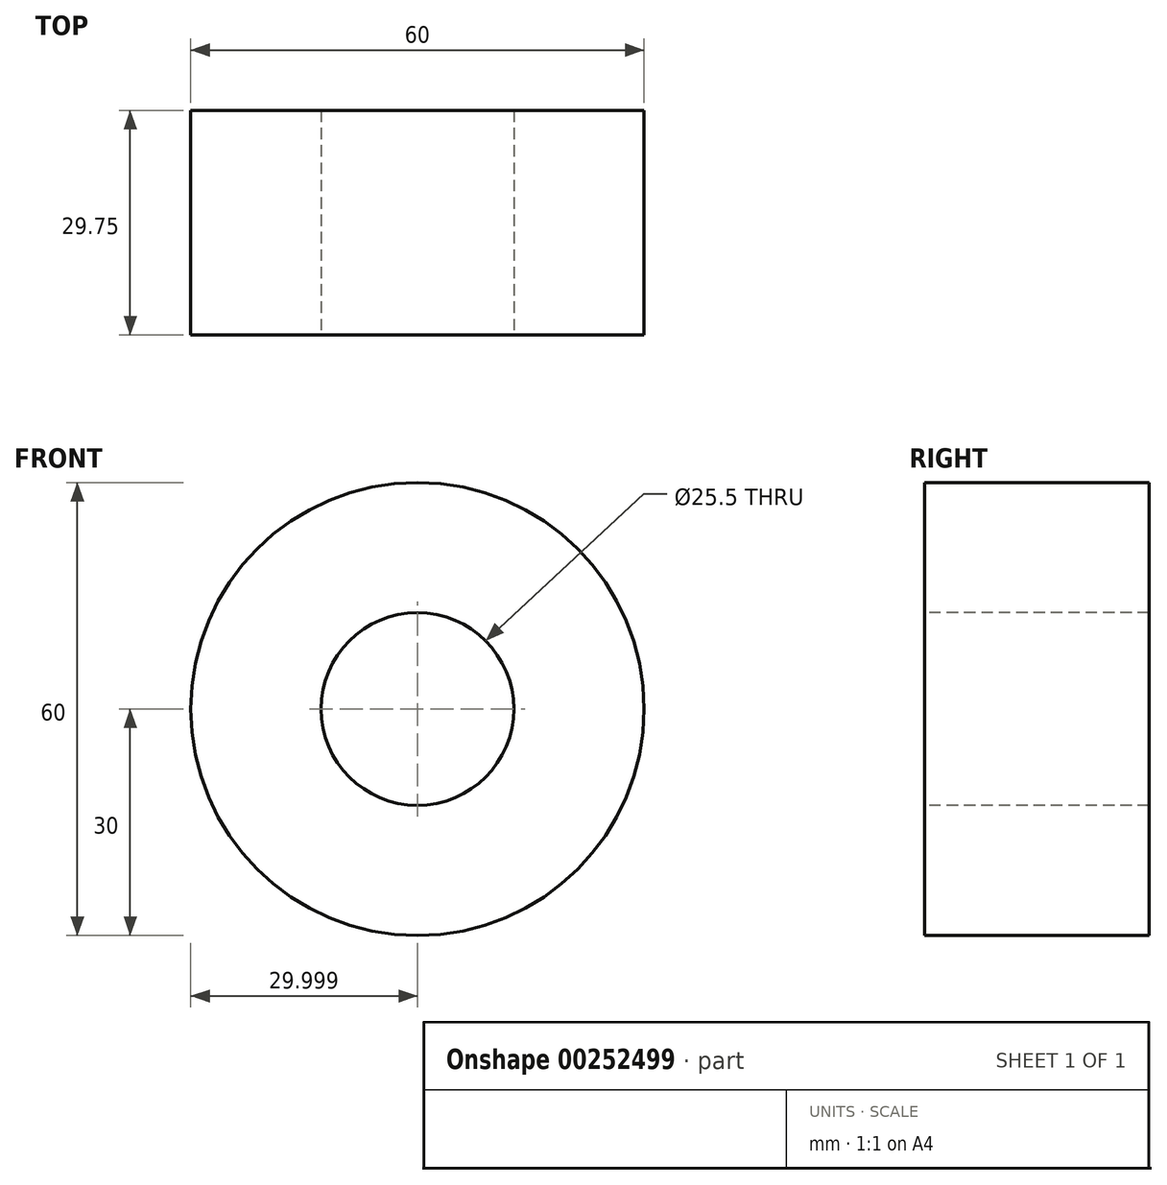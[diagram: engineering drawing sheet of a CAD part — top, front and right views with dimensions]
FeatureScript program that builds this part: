
annotation { "Feature Type Name" : "Feature", "Feature Type Description" : "" }
export const myFeature = defineFeature(function(context is Context, id is Id, definition is map)
    precondition{}
    {
        {
            var Q0;
            Q0=qCreatedBy(makeId("Front.planeOp"),FACE);
            var sketch = newSketch(context, id + "F0", { "sketchPlane" : qUnion([Q0])});
            skCircle(sketch, "E0", {"center": v(30.37, 30) * mm, "radius": 30 * mm});
            skCircle(sketch, "E1", {"center": v(30.37, 30) * mm, "radius": 12.75 * mm});
            skPoint(sketch, "E2", {"position": v(30.37, 0) * mm});
            skSolve(sketch);
        }
        {
            var Q0;
            Q0=qCreatedBy(makeId("Top.planeOp"),FACE);
            var sketch = newSketch(context, id + "F1", { "sketchPlane" : qUnion([Q0])});
            skLineSegment(sketch, "E3", {"start": v(-22.33, 0) * mm, "end": v(-22.33, 29.75) * mm, "construction": true});
            skSolve(sketch);
        }
        {
            var Q0;
            Q0=makeQuery(id+"F0.imprint","IMPRINT",FACE,{"disambiguationData":[TD([[makeQuery(id+"F0.imprint","IMPRINT",EDGE,{"derivedFrom":sQuery(id+"F0.wireOp",EDGE,"E0")}),1.0]])]});
            var Q1;
            Q1=sQuery(id+"F1.wireOp",VERTEX,"E3.end");
            extrude(context, id + "F2", {"entities" : qUnion([Q0]), "endBound" : BoundingType.UP_TO_VERTEX, "oppositeDirection" : true, "endBoundEntityVertex" : qUnion([Q1]), "depth" : 25 * mm});
        }
    });
